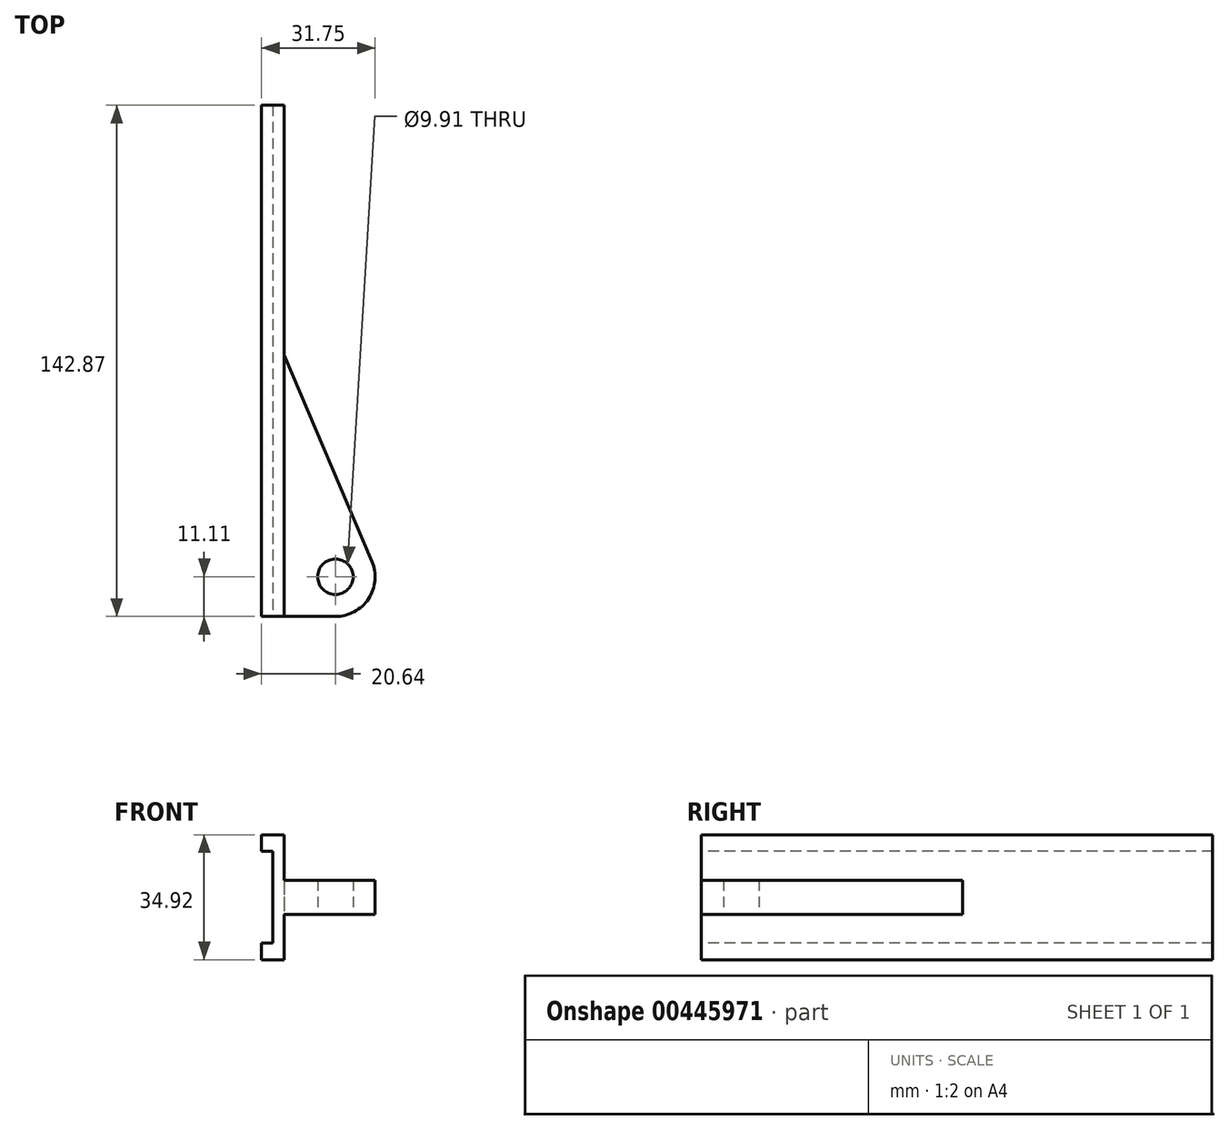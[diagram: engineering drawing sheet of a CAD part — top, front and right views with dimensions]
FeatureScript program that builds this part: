
annotation { "Feature Type Name" : "Feature", "Feature Type Description" : "" }
export const myFeature = defineFeature(function(context is Context, id is Id, definition is map)
    precondition{}
    {
        {
            var Q0;
            Q0=qCreatedBy(makeId("Top.planeOp"),FACE);
            var sketch = newSketch(context, id + "F0", { "sketchPlane" : qUnion([Q0])});
            skCircle(sketch, "E0", {"center": v(0, 0) * mm, "radius": 4.95 * mm});
            skLineSegment(sketch, "E1.bottom", {"start": v(0, 11.11) * mm, "end": v(-14.29, 11.11) * mm});
            skLineSegment(sketch, "E1.top", {"start": v(0, -11.11) * mm, "end": v(-14.29, -11.11) * mm});
            skLineSegment(sketch, "E1.right", {"start": v(-14.29, 11.11) * mm, "end": v(-14.29, -11.11) * mm});
            skPoint(sketch, "E1.middle", {"position": v(-7.14, 0) * mm});
            skArc(sketch, "E2", {"start": v(0, -11.11) * mm, "mid": v(11.11, 0) * mm, "end": v(0, 11.11) * mm});
            skLineSegment(sketch, "E3.bottom", {"start": v(-14.29, -11.11) * mm, "end": v(-20.64, -11.11) * mm});
            skLineSegment(sketch, "E3.top", {"start": v(-14.29, 131.76) * mm, "end": v(-20.64, 131.76) * mm});
            skLineSegment(sketch, "E3.left", {"start": v(-14.29, -11.11) * mm, "end": v(-14.29, 131.76) * mm});
            skLineSegment(sketch, "E3.right", {"start": v(-20.64, -11.11) * mm, "end": v(-20.64, 131.76) * mm});
            skPoint(sketch, "E3.middle", {"position": v(-35.27, 0) * mm});
            skLineSegment(sketch, "E4", {"start": v(-14.29, 49.21) * mm, "end": v(9.75, 5.34) * mm});
            skSolve(sketch);
        }
        {
            var Q0;
            Q0=makeQuery(id+"F0.imprint","IMPRINT",FACE,{"disambiguationData":[TD([[makeQuery(id+"F0.imprint","IMPRINT",EDGE,{"derivedFrom":sQuery(id+"F0.wireOp",EDGE,"E0")}),-1.0]])]});
            extrude(context, id + "F1", {"entities" : qUnion([Q0]), "endBound" : BoundingType.SYMMETRIC, "depth" : 9.52 * mm});
        }
        {
            var Q0;
            Q0=makeQuery(id+"F0.imprint","IMPRINT",FACE,{"disambiguationData":[TD([[makeQuery(id+"F0.imprint","IMPRINT",EDGE,{"derivedFrom":sQuery(id+"F0.wireOp",EDGE,"E3.bottom")}),-1.0]])]});
            extrude(context, id + "F2", {"entities" : qUnion([Q0]), "operationType" : NewBodyOperationType.ADD, "endBound" : BoundingType.SYMMETRIC, "depth" : 34.92 * mm});
        }
        {
            var Q0;
            Q0=makeQuery(id+"F2.opExtrude","SWEPT_FACE",FACE,{"disambiguationData":[OSD([sQuery(id+"F0.wireOp",EDGE,"E3.right")])]});
            var sketch = newSketch(context, id + "F3", { "sketchPlane" : qUnion([Q0])});
            skLineSegment(sketch, "E5.bottom", {"start": v(-131.76, -12.83) * mm, "end": v(11.11, -12.83) * mm});
            skLineSegment(sketch, "E5.top", {"start": v(-131.76, 12.83) * mm, "end": v(11.11, 12.83) * mm});
            skLineSegment(sketch, "E5.left", {"start": v(-131.76, -12.83) * mm, "end": v(-131.76, 12.83) * mm});
            skLineSegment(sketch, "E5.right", {"start": v(11.11, -12.83) * mm, "end": v(11.11, 12.83) * mm});
            skPoint(sketch, "E5.middle", {"position": v(11.11, 0) * mm});
            skLineSegment(sketch, "E6", {"start": v(11.11, 0) * mm, "end": v(-131.76, 0) * mm, "construction": true});
            skSolve(sketch);
        }
        {
            var Q0;
            Q0 = qSketchRegion(id + "F3", true);
            extrude(context, id + "F4", {"entities" : qUnion([Q0]), "operationType" : NewBodyOperationType.REMOVE, "oppositeDirection" : true, "depth" : 3.17 * mm});
        }
        {
            var Q0;
            Q0=qCreatedBy(makeId("Top.planeOp"),FACE);
            var sketch = newSketch(context, id + "F5", { "sketchPlane" : qUnion([Q0])});
            skLineSegment(sketch, "E7", {"start": v(0, 11.11) * mm, "end": v(-14.29, 11.11) * mm});
            skLineSegment(sketch, "E8", {"start": v(-14.29, 11.11) * mm, "end": v(-14.29, 61.91) * mm});
            skLineSegment(sketch, "E9", {"start": v(-14.29, 61.91) * mm, "end": v(10.22, 4.35) * mm});
            skArc(sketch, "E10", {"start": v(10.22, 4.35) * mm, "mid": v(6.13, 9.27) * mm, "end": v(0, 11.11) * mm});
            skSolve(sketch);
        }
        {
            var Q0;
            {var subQ0=sQuery(id+"F5.wireOp",EDGE,"E7");Q0=makeQuery(id+"F5.imprint","IMPRINT",FACE,{"disambiguationData":[TD([[makeQuery(id+"F5.imprint","IMPRINT",EDGE,{"derivedFrom":subQ0}),-1.0]])]});}
            extrude(context, id + "F6", {"entities" : qUnion([Q0]), "endBound" : BoundingType.SYMMETRIC, "depth" : 9.52 * mm});
        }
        {
            var Q0;
            Q0=makeQuery(id+"F6.opExtrude","SWEPT_BODY",BODY,{"disambiguationData":[OSD([sQuery(id+"F5.wireOp",EDGE,"E7"),sQuery(id+"F5.wireOp",EDGE,"E8"),sQuery(id+"F5.wireOp",EDGE,"E9"),sQuery(id+"F5.wireOp",EDGE,"E10")])]});
            deleteBodies(context, id + "F7", {"entities" : qUnion([Q0])});
        }
        {
            var Q0;
            Q0=makeQuery(id+"F5.imprint","IMPRINT",FACE,{"disambiguationData":[TD([[makeQuery(id+"F5.imprint","IMPRINT",EDGE,{"derivedFrom":sQuery(id+"F5.wireOp",EDGE,"E7")}),-1.0]])]});
            var Q1;
            Q1=sQuery(id+"F5.wireOp",EDGE,"E9");
            var Q2;
            Q2=sQuery(id+"F5.wireOp",EDGE,"E8");
            var Q3;
            Q3=sQuery(id+"F5.wireOp",EDGE,"E7");
            var Q4;
            Q4=sQuery(id+"F5.wireOp",EDGE,"E10");
            extrude(context, id + "F8", {"entities" : qUnion([Q0]), "operationType" : NewBodyOperationType.ADD, "surfaceEntities" : qUnion([Q1, Q2, Q3, Q4]), "endBound" : BoundingType.SYMMETRIC, "depth" : 9.52 * mm});
        }
    });
